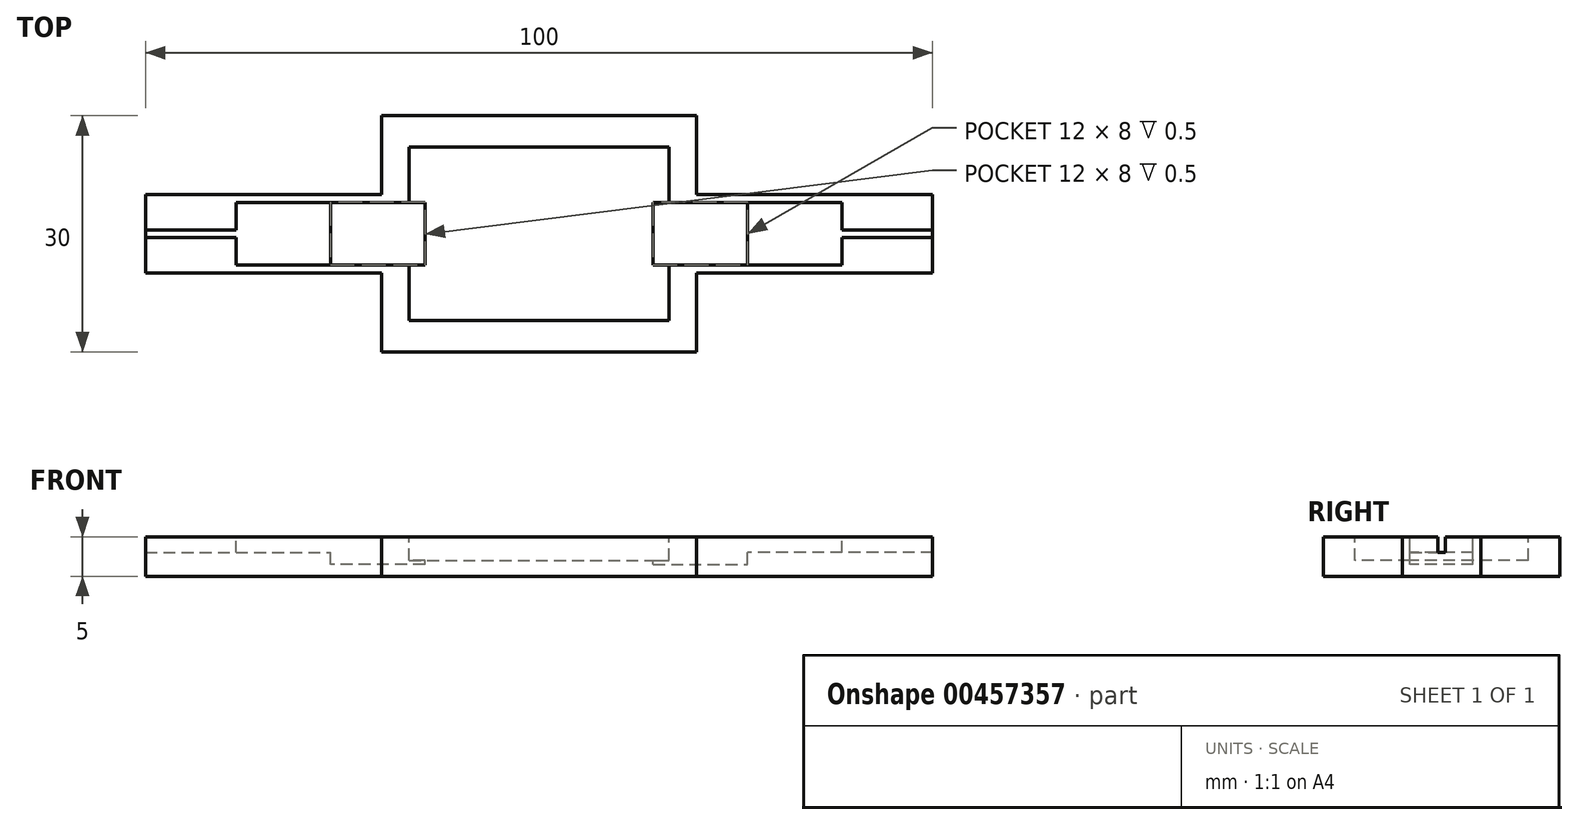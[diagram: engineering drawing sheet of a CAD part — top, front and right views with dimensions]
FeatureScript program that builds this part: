
annotation { "Feature Type Name" : "Feature", "Feature Type Description" : "" }
export const myFeature = defineFeature(function(context is Context, id is Id, definition is map)
    precondition{}
    {
        {
            var Q0;
            Q0=qCreatedBy(makeId("Top.planeOp"),FACE);
            var sketch = newSketch(context, id + "F0", { "sketchPlane" : qUnion([Q0])});
            skLineSegment(sketch, "E0", {"start": v(-20, -15) * mm, "end": v(20, -15) * mm});
            skLineSegment(sketch, "E1", {"start": v(20, -15) * mm, "end": v(20, -5) * mm});
            skLineSegment(sketch, "E2", {"start": v(20, -5) * mm, "end": v(50, -5) * mm});
            skLineSegment(sketch, "E3", {"start": v(50, -5) * mm, "end": v(50, 5) * mm});
            skLineSegment(sketch, "E4", {"start": v(20, 5) * mm, "end": v(20, 15) * mm});
            skLineSegment(sketch, "E5", {"start": v(-20, 15) * mm, "end": v(20, 15) * mm});
            skLineSegment(sketch, "E6", {"start": v(20, 5) * mm, "end": v(50, 5) * mm});
            skLineSegment(sketch, "E7", {"start": v(-20, 15) * mm, "end": v(-20, 5) * mm});
            skLineSegment(sketch, "E8", {"start": v(-20, 5) * mm, "end": v(-50, 5) * mm});
            skLineSegment(sketch, "E9", {"start": v(-50, -5) * mm, "end": v(-20, -5) * mm});
            skLineSegment(sketch, "E10", {"start": v(-20, -15) * mm, "end": v(-20, -5) * mm});
            skLineSegment(sketch, "E11", {"start": v(-50, 5) * mm, "end": v(-50, -5) * mm});
            skSolve(sketch);
        }
        {
            var Q0;
            Q0=qSketchRegion(id+"F0",true);
            extrude(context, id + "F1", {"entities" : qUnion([Q0]), "depth" : 5 * mm});
        }
        {
            var Q0;
            Q0=makeQuery(id+"F1.opExtrude","CAP_FACE",FACE,{"disambiguationData":[OSD([sQuery(id+"F0.wireOp",EDGE,"E0"),sQuery(id+"F0.wireOp",EDGE,"E1"),sQuery(id+"F0.wireOp",EDGE,"E2"),sQuery(id+"F0.wireOp",EDGE,"E3"),sQuery(id+"F0.wireOp",EDGE,"E4"),sQuery(id+"F0.wireOp",EDGE,"E5"),sQuery(id+"F0.wireOp",EDGE,"E6"),sQuery(id+"F0.wireOp",EDGE,"E7"),sQuery(id+"F0.wireOp",EDGE,"E8"),sQuery(id+"F0.wireOp",EDGE,"E9"),sQuery(id+"F0.wireOp",EDGE,"E10"),sQuery(id+"F0.wireOp",EDGE,"E11")])],"isStart":false});
            var sketch = newSketch(context, id + "F2", { "sketchPlane" : qUnion([Q0])});
            skLineSegment(sketch, "E12.bottom", {"start": v(-16.5, 11) * mm, "end": v(16.5, 11) * mm});
            skLineSegment(sketch, "E12.top", {"start": v(-16.5, -11) * mm, "end": v(16.5, -11) * mm});
            skLineSegment(sketch, "E12.left", {"start": v(-16.5, 11) * mm, "end": v(-16.5, -11) * mm});
            skLineSegment(sketch, "E12.right", {"start": v(16.5, 11) * mm, "end": v(16.5, -11) * mm});
            skLineSegment(sketch, "E13.bottom", {"start": v(14.5, 4) * mm, "end": v(16.5, 4) * mm});
            skLineSegment(sketch, "E13.top", {"start": v(14.5, -4) * mm, "end": v(16.5, -4) * mm});
            skLineSegment(sketch, "E13.left", {"start": v(14.5, 4) * mm, "end": v(14.5, -4) * mm});
            skLineSegment(sketch, "E13.right", {"start": v(16.5, 4) * mm, "end": v(16.5, -4) * mm});
            skLineSegment(sketch, "E14.bottom", {"start": v(-14.5, 4) * mm, "end": v(-16.5, 4) * mm});
            skLineSegment(sketch, "E14.top", {"start": v(-14.5, -4) * mm, "end": v(-16.5, -4) * mm});
            skLineSegment(sketch, "E14.left", {"start": v(-14.5, 4) * mm, "end": v(-14.5, -4) * mm});
            skLineSegment(sketch, "E14.right", {"start": v(-16.5, 4) * mm, "end": v(-16.5, -4) * mm});
            skLineSegment(sketch, "E15.left", {"start": v(-16.5, -4) * mm, "end": v(-16.5, 4) * mm});
            skSolve(sketch);
        }
        {
            var Q0;
            {var subQ7=sQuery(id+"F2.wireOp",EDGE,"E12.bottom");Q0=makeQuery(id+"F2.imprint","IMPRINT",FACE,{"disambiguationData":[TD([[makeQuery(id+"F2.imprint","IMPRINT",EDGE,{"derivedFrom":subQ7}),-1.0]])]});}
            extrude(context, id + "F3", {"entities" : qUnion([Q0]), "operationType" : NewBodyOperationType.REMOVE, "oppositeDirection" : true, "depth" : 3 * mm});
        }
        {
            var Q0;
            Q0=makeQuery(id+"F1.opExtrude","CAP_FACE",FACE,{"disambiguationData":[OSD([sQuery(id+"F0.wireOp",EDGE,"E0"),sQuery(id+"F0.wireOp",EDGE,"E1"),sQuery(id+"F0.wireOp",EDGE,"E2"),sQuery(id+"F0.wireOp",EDGE,"E3"),sQuery(id+"F0.wireOp",EDGE,"E4"),sQuery(id+"F0.wireOp",EDGE,"E5"),sQuery(id+"F0.wireOp",EDGE,"E6"),sQuery(id+"F0.wireOp",EDGE,"E7"),sQuery(id+"F0.wireOp",EDGE,"E8"),sQuery(id+"F0.wireOp",EDGE,"E9"),sQuery(id+"F0.wireOp",EDGE,"E10"),sQuery(id+"F0.wireOp",EDGE,"E11")])],"isStart":false});
            var sketch = newSketch(context, id + "F4", { "sketchPlane" : qUnion([Q0])});
            skLineSegment(sketch, "E16.bottom", {"start": v(-14.5, 4) * mm, "end": v(-26.5, 4) * mm});
            skLineSegment(sketch, "E16.top", {"start": v(-14.5, -4) * mm, "end": v(-26.5, -4) * mm});
            skLineSegment(sketch, "E16.left", {"start": v(-14.5, 4) * mm, "end": v(-14.5, -4) * mm});
            skLineSegment(sketch, "E16.right", {"start": v(-26.5, 4) * mm, "end": v(-26.5, -4) * mm});
            skPoint(sketch, "E17.oppositeSnap0", {"position": v(-20.5, -4) * mm});
            skLineSegment(sketch, "E17.bottom", {"start": v(14.5, 4) * mm, "end": v(26.5, 4) * mm});
            skLineSegment(sketch, "E17.top", {"start": v(14.5, -4) * mm, "end": v(26.5, -4) * mm});
            skLineSegment(sketch, "E17.left", {"start": v(14.5, 4) * mm, "end": v(14.5, -4) * mm});
            skLineSegment(sketch, "E17.right", {"start": v(26.5, 4) * mm, "end": v(26.5, -4) * mm});
            skSolve(sketch);
        }
        {
            var Q0;
            Q0 = qSketchRegion(id + "F4", true);
            extrude(context, id + "F5", {"entities" : qUnion([Q0]), "operationType" : NewBodyOperationType.REMOVE, "oppositeDirection" : true, "depth" : 3.5 * mm});
        }
        {
            var Q0;
            Q0=makeQuery(id+"F1.opExtrude","CAP_FACE",FACE,{"disambiguationData":[OSD([sQuery(id+"F0.wireOp",EDGE,"E0"),sQuery(id+"F0.wireOp",EDGE,"E1"),sQuery(id+"F0.wireOp",EDGE,"E2"),sQuery(id+"F0.wireOp",EDGE,"E3"),sQuery(id+"F0.wireOp",EDGE,"E4"),sQuery(id+"F0.wireOp",EDGE,"E5"),sQuery(id+"F0.wireOp",EDGE,"E6"),sQuery(id+"F0.wireOp",EDGE,"E7"),sQuery(id+"F0.wireOp",EDGE,"E8"),sQuery(id+"F0.wireOp",EDGE,"E9"),sQuery(id+"F0.wireOp",EDGE,"E10"),sQuery(id+"F0.wireOp",EDGE,"E11")])],"isStart":false});
            var sketch = newSketch(context, id + "F6", { "sketchPlane" : qUnion([Q0])});
            skLineSegment(sketch, "E18.bottom", {"start": v(-38.5, -4) * mm, "end": v(-26.5, -4) * mm});
            skLineSegment(sketch, "E18.top", {"start": v(-38.5, 4) * mm, "end": v(-26.5, 4) * mm});
            skLineSegment(sketch, "E18.left", {"start": v(-38.5, -4) * mm, "end": v(-38.5, 4) * mm});
            skLineSegment(sketch, "E18.right", {"start": v(-26.5, -4) * mm, "end": v(-26.5, 4) * mm});
            skLineSegment(sketch, "E19.bottom", {"start": v(38.5, -4) * mm, "end": v(26.5, -4) * mm});
            skLineSegment(sketch, "E19.top", {"start": v(38.5, 4) * mm, "end": v(26.5, 4) * mm});
            skLineSegment(sketch, "E19.left", {"start": v(38.5, -4) * mm, "end": v(38.5, 4) * mm});
            skLineSegment(sketch, "E19.right", {"start": v(26.5, -4) * mm, "end": v(26.5, 4) * mm});
            skSolve(sketch);
        }
        {
            var Q0;
            Q0=makeQuery(id+"F6.imprint","IMPRINT",FACE,{"disambiguationData":[TD([[makeQuery(id+"F6.imprint","IMPRINT",EDGE,{"derivedFrom":sQuery(id+"F6.wireOp",EDGE,"E18.bottom")}),1.0]])]});
            var Q1;
            Q1=makeQuery(id+"F6.imprint","IMPRINT",FACE,{"disambiguationData":[TD([[makeQuery(id+"F6.imprint","IMPRINT",EDGE,{"derivedFrom":sQuery(id+"F6.wireOp",EDGE,"E19.bottom")}),-1.0]])]});
            extrude(context, id + "F7", {"entities" : qUnion([Q0, Q1]), "operationType" : NewBodyOperationType.REMOVE, "oppositeDirection" : true, "depth" : 2 * mm});
        }
        {
            var Q0;
            Q0=makeQuery(id+"F1.opExtrude","CAP_FACE",FACE,{"disambiguationData":[OSD([sQuery(id+"F0.wireOp",EDGE,"E0"),sQuery(id+"F0.wireOp",EDGE,"E1"),sQuery(id+"F0.wireOp",EDGE,"E2"),sQuery(id+"F0.wireOp",EDGE,"E3"),sQuery(id+"F0.wireOp",EDGE,"E4"),sQuery(id+"F0.wireOp",EDGE,"E5"),sQuery(id+"F0.wireOp",EDGE,"E6"),sQuery(id+"F0.wireOp",EDGE,"E7"),sQuery(id+"F0.wireOp",EDGE,"E8"),sQuery(id+"F0.wireOp",EDGE,"E9"),sQuery(id+"F0.wireOp",EDGE,"E10"),sQuery(id+"F0.wireOp",EDGE,"E11")])],"isStart":false});
            var sketch = newSketch(context, id + "F8", { "sketchPlane" : qUnion([Q0])});
            skLineSegment(sketch, "E20.bottom", {"start": v(-50, -0.5) * mm, "end": v(-38.5, -0.5) * mm});
            skLineSegment(sketch, "E20.top", {"start": v(-50, 0.5) * mm, "end": v(-38.5, 0.5) * mm});
            skLineSegment(sketch, "E20.left", {"start": v(-50, -0.5) * mm, "end": v(-50, 0.5) * mm});
            skLineSegment(sketch, "E20.right", {"start": v(-38.5, -0.5) * mm, "end": v(-38.5, 0.5) * mm});
            skLineSegment(sketch, "E21.bottom", {"start": v(50, -0.5) * mm, "end": v(38.5, -0.5) * mm});
            skLineSegment(sketch, "E21.top", {"start": v(50, 0.5) * mm, "end": v(38.5, 0.5) * mm});
            skLineSegment(sketch, "E21.left", {"start": v(50, -0.5) * mm, "end": v(50, 0.5) * mm});
            skLineSegment(sketch, "E21.right", {"start": v(38.5, -0.5) * mm, "end": v(38.5, 0.5) * mm});
            skSolve(sketch);
        }
        {
            var Q0;
            Q0 = qSketchRegion(id + "F8", true);
            extrude(context, id + "F9", {"entities" : qUnion([Q0]), "operationType" : NewBodyOperationType.REMOVE, "oppositeDirection" : true, "depth" : 2 * mm});
        }
    });
